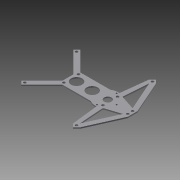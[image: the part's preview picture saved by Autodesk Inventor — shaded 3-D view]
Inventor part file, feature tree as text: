
AUTODESK INVENTOR PART (.ipt)
format: ipt  version: 2013 (Build 170138000, 138)  size: 235,008 bytes
history: native  units: in
note: dims shown in document units (in); Inventor stores cm internally (conversion verified against a paired STEP export)
features: extrude x7, sketch x7, reference x2
ambient origin geometry x8: Origin, YZ Plane, XZ Plane, XY Plane, X Axis, Y Axis, Z Axis, Center Point
feature tree (16):
  extrude  "Extrusion3"  Depth=0.748in
  extrude  "Extrusion4"  Depth=1.6in
  extrude  "Extrusion5"  Depth=1.125in
  extrude  "Extrusion6"  Depth=0.125in TaperAngle=0.0deg
  extrude  "Extrusion7"  Depth=0.266in
  extrude  "Extrusion8"  Depth=0.25in
  extrude  "Extrusion9"  Depth=0.25in
  sketch  "Sketch1"  dims[d3=2.0in d4=0.748in]
  sketch  "Sketch2"  dims[d12=1.125in d13=1.6in]
  sketch  "Sketch3"  dims[d14=4.5in d15=1.125in]
  sketch  "Sketch4"  dims[d16=1.6in d17=0.125in d18=0.0in]
  reference  "Reference1"
  sketch  "Sketch5"  dims[d19=0.266in d20=0.266in]
  sketch  "Sketch6"  dims[d21=0.25in d22=0.25in]
  sketch  "Sketch7"  dims[d23=0.25in d24=0.25in d25=1.0in d26=0.0in d27=0.266in d28=0.266in d29=0.25in d30=0.25in d31=0.25in d32=0.25in d33=1.0in d34=0.0in d35=0.25in d36=0.125in d39=0.5in d40=0.5in d41=0.125in d42=0.0in d47=2.375in d48=0.125in d49=0.0in d51=0.16in d52=0.16in d53=0.16in d54=0.125in d55=0.0in d56=0.8in d57=1.0in d58=1.0in d59=1.0in d60=0.125in d61=0.0in]
  reference  "Reference2"
